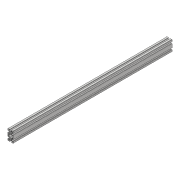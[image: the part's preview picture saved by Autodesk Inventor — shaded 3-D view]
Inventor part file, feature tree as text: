
AUTODESK INVENTOR PART (.ipt)
format: ipt  version: 2018 (Build 220112000, 112)  size: 239,616 bytes
history: native  units: mm
features: extrude x1, sketch x1
ambient origin geometry x8: Origin, YZ Plane, XZ Plane, XY Plane, X Axis, Y Axis, Z Axis, Center Point
bodies: Solid1 (feature_tree)
feature tree (2):
  extrude  "Extrusion1"  [1 undecoded]
  sketch  "Sketch1"  dims[d0=600.0mm d1=0.0mm]
note: 1 required parameter value undecoded (feature->parameter linkage not recoverable at this tier; creation-order binding heuristic only, values carry confidence <= 0.55)
